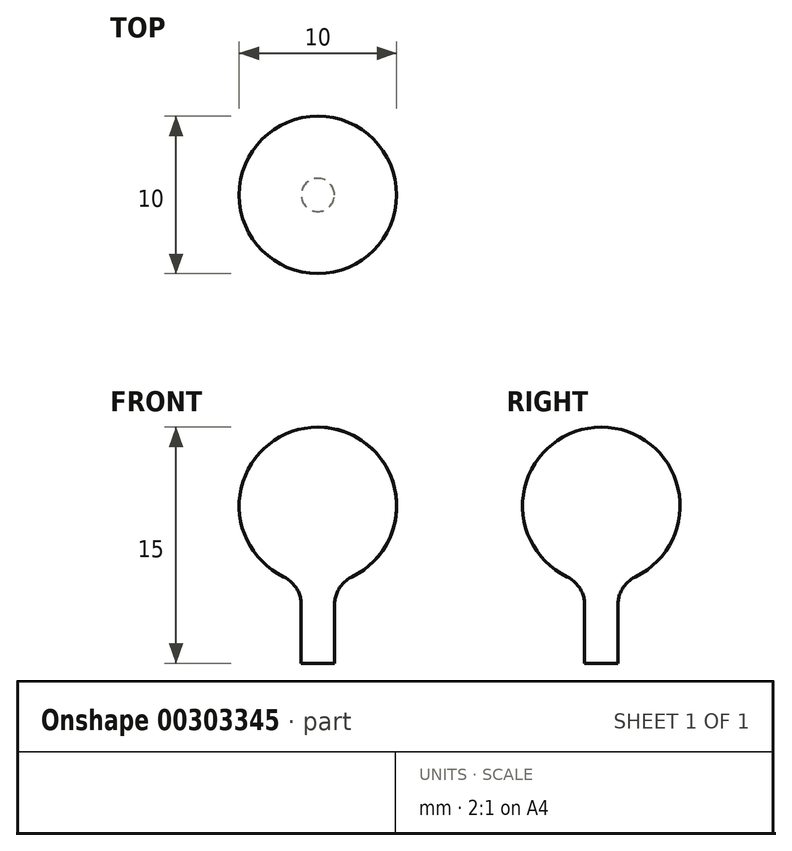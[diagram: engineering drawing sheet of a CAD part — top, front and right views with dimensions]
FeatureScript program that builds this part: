
annotation { "Feature Type Name" : "Feature", "Feature Type Description" : "" }
export const myFeature = defineFeature(function(context is Context, id is Id, definition is map)
    precondition{}
    {
        {
            var Q0;
            Q0=qCreatedBy(makeId("Front.planeOp"),FACE);
            var sketch = newSketch(context, id + "F0", { "sketchPlane" : qUnion([Q0])});
            skArc(sketch, "E0", {"start": v(1.06, -4.89) * mm, "mid": v(4.97, 0.53) * mm, "end": v(0, 5) * mm});
            skLineSegment(sketch, "E1.top", {"start": v(1.06, -10) * mm, "end": v(0, -10) * mm});
            skLineSegment(sketch, "E1.left", {"start": v(1.06, -4.89) * mm, "end": v(1.06, -10) * mm});
            skPoint(sketch, "E2.orphan", {"position": v(1.06, 10) * mm});
            skPoint(sketch, "E3.orphan", {"position": v(-1.06, 10) * mm});
            skLineSegment(sketch, "E4", {"start": v(0, 5) * mm, "end": v(0, -10) * mm});
            skPoint(sketch, "E5.orphan", {"position": v(-1.06, -10) * mm});
            skLineSegment(sketch, "E6", {"start": v(0, 8.85) * mm, "end": v(0, -22.23) * mm, "construction": true});
            skSolve(sketch);
        }
        {
            var Q0;
            Q0 = qSketchRegion(id + "F0", true);
            var Q1;
            Q1=sQuery(id+"F0.wireOp",EDGE,"E6");
            revolve(context, id + "F1", {"entities" : qUnion([Q0]), "axis" : qUnion([Q1]), "revolveType" : RevolveType.FULL});
        }
        {
            var Q0;
            Q0=makeQuery(id+"F1.opRevolve","SWEPT_FACE",FACE,{"disambiguationData":[OSD([sQuery(id+"F0.wireOp",EDGE,"E0")])]});
            fillet(context, id + "F2", {"entities" : qUnion([Q0]), "radius" : 2 * mm, "tangentPropagation" : true, "allowEdgeOverflow" : false});
        }
    });
